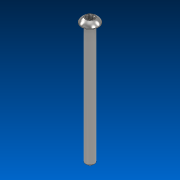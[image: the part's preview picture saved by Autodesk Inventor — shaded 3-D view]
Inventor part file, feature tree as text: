
AUTODESK INVENTOR PART (.ipt)
format: ipt  version: 2022.2 (Build 262287000, 287)  size: 151,040 bytes
history: native  units: in
note: dims shown in document units (in); Inventor stores cm internally (conversion verified against a paired STEP export)
features: chamfer x1
ambient origin geometry x8: Origin, YZ Plane, XZ Plane, XY Plane, X Axis, Y Axis, Z Axis, Center Point
bodies: Solid1 (feature_tree)
feature tree (1):
  chamfer  "Chamfer2"  [1 undecoded]
note: 1 required parameter value undecoded (feature->parameter linkage not recoverable at this tier; creation-order binding heuristic only, values carry confidence <= 0.55)
